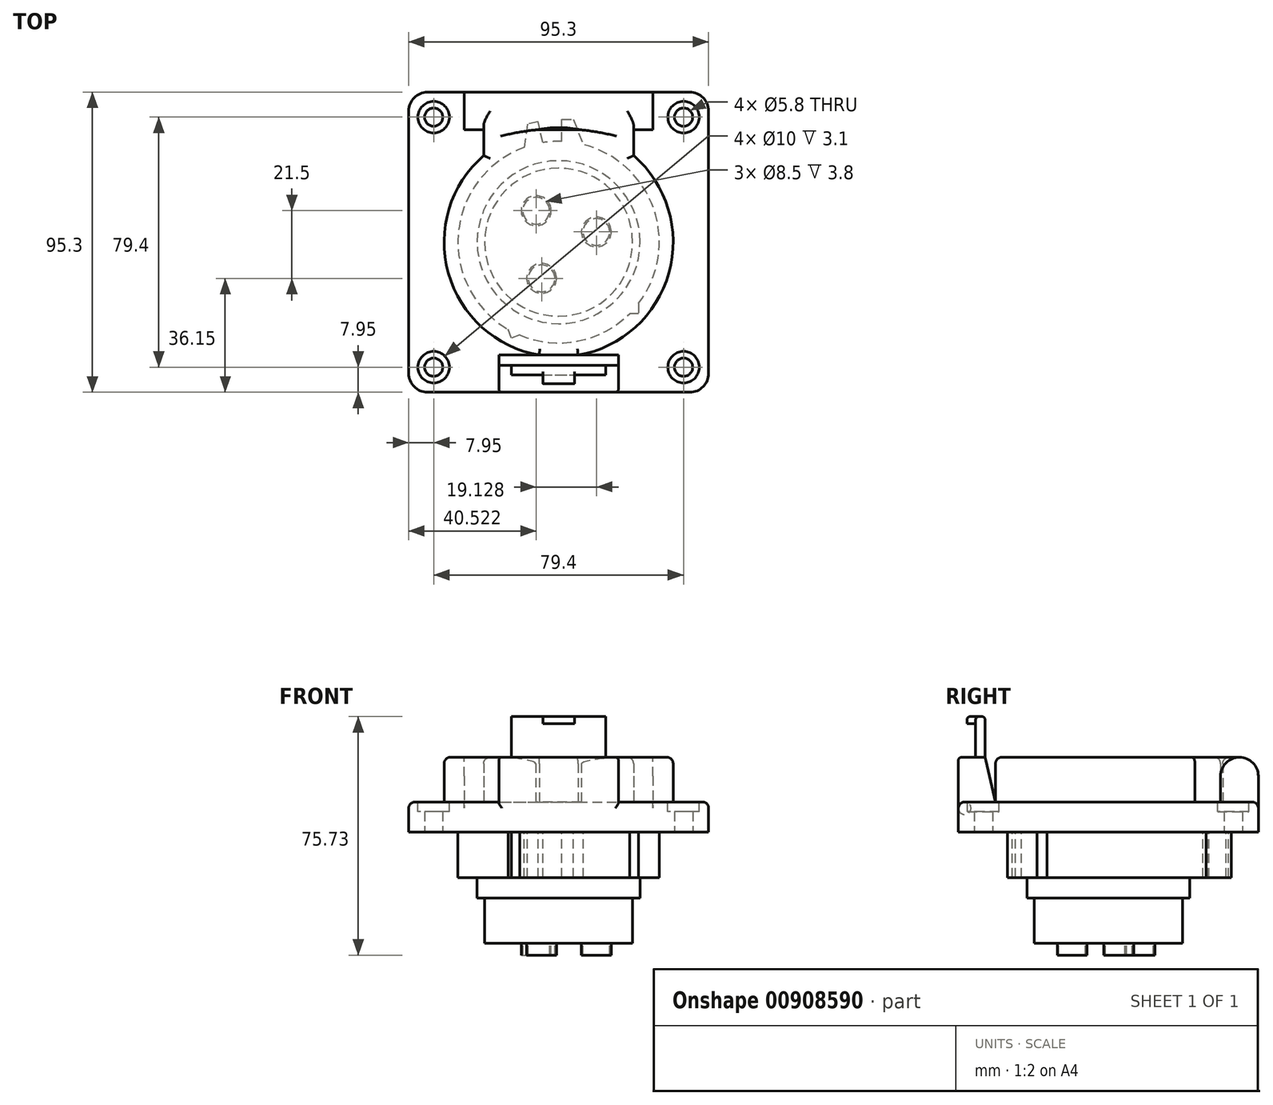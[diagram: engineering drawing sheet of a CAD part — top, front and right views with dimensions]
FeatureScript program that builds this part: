
annotation { "Feature Type Name" : "Feature", "Feature Type Description" : "" }
export const myFeature = defineFeature(function(context is Context, id is Id, definition is map)
    precondition{}
    {
        {
            var Q0;
            Q0=qCreatedBy(makeId("Top.planeOp"),FACE);
            var sketch = newSketch(context, id + "F0", { "sketchPlane" : qUnion([Q0])});
            skLineSegment(sketch, "E0.bottom", {"start": v(47.65, -47.65) * mm, "end": v(-47.65, -47.65) * mm});
            skLineSegment(sketch, "E0.top", {"start": v(47.65, 47.65) * mm, "end": v(-47.65, 47.65) * mm});
            skLineSegment(sketch, "E0.left", {"start": v(47.65, -47.65) * mm, "end": v(47.65, 47.65) * mm});
            skLineSegment(sketch, "E0.right", {"start": v(-47.65, -47.65) * mm, "end": v(-47.65, 47.65) * mm});
            skPoint(sketch, "E0.middle", {"position": v(0, 0) * mm});
            skSolve(sketch);
        }
        {
            var Q0;
            Q0=makeQuery(id+"F0.imprint","IMPRINT",FACE,{"disambiguationData":[TD([[makeQuery(id+"F0.imprint","IMPRINT",EDGE,{"derivedFrom":sQuery(id+"F0.wireOp",EDGE,"E0.bottom")}),-1.0]])]});
            extrude(context, id + "F1", {"entities" : qUnion([Q0]), "depth" : 9.5 * mm, "offsetDistance" : 25 * mm});
        }
        {
            var Q0;
            Q0=makeQuery(id+"F1.opExtrude","CAP_FACE",FACE,{"disambiguationData":[OSD([sQuery(id+"F0.wireOp",EDGE,"E0.bottom"),sQuery(id+"F0.wireOp",EDGE,"E0.top"),sQuery(id+"F0.wireOp",EDGE,"E0.left"),sQuery(id+"F0.wireOp",EDGE,"E0.right")])],"isStart":true});
            var sketch = newSketch(context, id + "F2", { "sketchPlane" : qUnion([Q0])});
            skCircle(sketch, "E1", {"center": v(0, 0) * mm, "radius": 32 * mm});
            skLineSegment(sketch, "E2", {"start": v(1.02, -31.98) * mm, "end": v(1.02, -39) * mm});
            skLineSegment(sketch, "E3", {"start": v(1.02, -39) * mm, "end": v(4.66, -39) * mm});
            skLineSegment(sketch, "E4", {"start": v(4.66, -39) * mm, "end": v(7.84, -31.02) * mm});
            skLineSegment(sketch, "E5", {"start": v(-5.04, -31.6) * mm, "end": v(-6.48, -38.2) * mm});
            skLineSegment(sketch, "E6", {"start": v(-6.48, -38.2) * mm, "end": v(-9.9, -37.45) * mm});
            skLineSegment(sketch, "E7", {"start": v(-9.9, -37.45) * mm, "end": v(-10.91, -30.08) * mm});
            skLineSegment(sketch, "E8", {"start": v(25.4, 19.47) * mm, "end": v(25.4, 22.7) * mm});
            skLineSegment(sketch, "E9", {"start": v(25.4, 22.7) * mm, "end": v(22.56, 22.7) * mm});
            skLineSegment(sketch, "E10", {"start": v(-12.39, 29.5) * mm, "end": v(-14.98, 30.5) * mm});
            skLineSegment(sketch, "E11", {"start": v(-14.98, 30.5) * mm, "end": v(-16.08, 27.67) * mm});
            skSolve(sketch);
        }
        {
            var Q0;
            {var subQ0=sQuery(id+"F2.wireOp",EDGE,"E1");var subQ5=makeQuery(id+"F2.imprint","INTERSECT",VERTEX,{"derivedFrom":[subQ0,sQuery(id+"F2.wireOp",EDGE,"E8")]});Q0=makeQuery(id+"F2.imprint","IMPRINT",FACE,{"disambiguationData":[TD([[makeQuery(id+"F2.imprint","IMPRINT",EDGE,{"disambiguationData":[TD([[subQ5,-1.0]])],"derivedFrom":subQ0}),1.0]])]});}
            var Q1;
            {var subQ0=sQuery(id+"F2.wireOp",EDGE,"E8");Q1=makeQuery(id+"F2.imprint","IMPRINT",FACE,{"disambiguationData":[TD([[makeQuery(id+"F2.imprint","IMPRINT",EDGE,{"derivedFrom":subQ0}),1.0]])]});}
            var Q2;
            {var subQ0=sQuery(id+"F2.wireOp",EDGE,"E10");Q2=makeQuery(id+"F2.imprint","IMPRINT",FACE,{"disambiguationData":[TD([[makeQuery(id+"F2.imprint","IMPRINT",EDGE,{"derivedFrom":subQ0}),1.0]])]});}
            var Q3;
            {var subQ0=sQuery(id+"F2.wireOp",EDGE,"E2");Q3=makeQuery(id+"F2.imprint","IMPRINT",FACE,{"disambiguationData":[TD([[makeQuery(id+"F2.imprint","IMPRINT",EDGE,{"derivedFrom":subQ0}),1.0]])]});}
            var Q4;
            {var subQ0=sQuery(id+"F2.wireOp",EDGE,"E5");Q4=makeQuery(id+"F2.imprint","IMPRINT",FACE,{"disambiguationData":[TD([[makeQuery(id+"F2.imprint","IMPRINT",EDGE,{"derivedFrom":subQ0}),-1.0]])]});}
            extrude(context, id + "F3", {"entities" : qUnion([Q0, Q1, Q2, Q3, Q4]), "operationType" : NewBodyOperationType.ADD, "depth" : 14.5 * mm, "offsetDistance" : 25 * mm});
        }
        {
            var Q0;
            Q0=makeQuery(id+"F3.opExtrude","CAP_FACE",FACE,{"disambiguationData":[OSD([sQuery(id+"F2.wireOp",EDGE,"E1"),sQuery(id+"F2.wireOp",EDGE,"E2"),sQuery(id+"F2.wireOp",EDGE,"E3"),sQuery(id+"F2.wireOp",EDGE,"E4"),sQuery(id+"F2.wireOp",EDGE,"E5"),sQuery(id+"F2.wireOp",EDGE,"E6"),sQuery(id+"F2.wireOp",EDGE,"E7"),sQuery(id+"F2.wireOp",EDGE,"E8"),sQuery(id+"F2.wireOp",EDGE,"E9"),sQuery(id+"F2.wireOp",EDGE,"E10"),sQuery(id+"F2.wireOp",EDGE,"E11")])],"isStart":false});
            var sketch = newSketch(context, id + "F4", { "sketchPlane" : qUnion([Q0])});
            skCircle(sketch, "E12", {"center": v(0, 0) * mm, "radius": 25.88 * mm});
            skSolve(sketch);
        }
        {
            var Q0;
            Q0 = qSketchRegion(id + "F4", true);
            extrude(context, id + "F5", {"entities" : qUnion([Q0]), "operationType" : NewBodyOperationType.ADD, "depth" : 6.5 * mm, "offsetDistance" : 25 * mm});
        }
        {
            var Q0;
            Q0=makeQuery(id+"F5.opExtrude","CAP_FACE",FACE,{"disambiguationData":[OSD([sQuery(id+"F4.wireOp",EDGE,"E12")])],"isStart":false});
            var sketch = newSketch(context, id + "F6", { "sketchPlane" : qUnion([Q0])});
            skCircle(sketch, "E13", {"center": v(0, 0) * mm, "radius": 23.5 * mm});
            skSolve(sketch);
        }
        {
            var Q0;
            Q0 = qSketchRegion(id + "F6", true);
            extrude(context, id + "F7", {"entities" : qUnion([Q0]), "operationType" : NewBodyOperationType.ADD, "depth" : 14.33 * mm, "offsetDistance" : 25 * mm});
        }
        {
            var Q0;
            Q0=makeQuery(id+"F7.opExtrude","CAP_FACE",FACE,{"disambiguationData":[OSD([sQuery(id+"F6.wireOp",EDGE,"E13")])],"isStart":false});
            var sketch = newSketch(context, id + "F8", { "sketchPlane" : qUnion([Q0])});
            skCircle(sketch, "E14", {"center": v(-7.13, -10) * mm, "radius": 4.75 * mm});
            skCircle(sketch, "E15", {"center": v(-5.4, 11.5) * mm, "radius": 4.75 * mm});
            skCircle(sketch, "E16", {"center": v(12, -3.26) * mm, "radius": 4.75 * mm});
            skCircle(sketch, "E17", {"center": v(12, -3.26) * mm, "radius": 4.25 * mm});
            skCircle(sketch, "E18", {"center": v(-7.13, -10) * mm, "radius": 4.25 * mm});
            skCircle(sketch, "E19", {"center": v(-5.4, 11.5) * mm, "radius": 4.25 * mm});
            skSolve(sketch);
        }
        {
            var Q0;
            Q0 = qSketchRegion(id + "F8", true);
            extrude(context, id + "F9", {"entities" : qUnion([Q0]), "operationType" : NewBodyOperationType.ADD, "depth" : 3.8 * mm, "offsetDistance" : 25 * mm});
        }
        {
            var Q0;
            Q0=makeQuery(id+"F1.opExtrude","CAP_FACE",FACE,{"disambiguationData":[OSD([sQuery(id+"F0.wireOp",EDGE,"E0.bottom"),sQuery(id+"F0.wireOp",EDGE,"E0.top"),sQuery(id+"F0.wireOp",EDGE,"E0.left"),sQuery(id+"F0.wireOp",EDGE,"E0.right")])],"isStart":false});
            var sketch = newSketch(context, id + "F10", { "sketchPlane" : qUnion([Q0])});
            skLineSegment(sketch, "E20.bottom", {"start": v(-30, 47.65) * mm, "end": v(30, 47.65) * mm});
            skLineSegment(sketch, "E20.top", {"start": v(-30, 35.65) * mm, "end": v(30, 35.65) * mm});
            skLineSegment(sketch, "E20.left", {"start": v(-30, 47.65) * mm, "end": v(-30, 35.65) * mm});
            skLineSegment(sketch, "E20.right", {"start": v(30, 47.65) * mm, "end": v(30, 35.65) * mm});
            skCircle(sketch, "E21", {"center": v(0, 0) * mm, "radius": 36.38 * mm});
            skLineSegment(sketch, "E22", {"start": v(-23.8, 35.65) * mm, "end": v(-23.8, 27.5) * mm});
            skLineSegment(sketch, "E23", {"start": v(23.8, 35.65) * mm, "end": v(23.8, 27.5) * mm});
            skLineSegment(sketch, "E24.bottom", {"start": v(-19, -47.65) * mm, "end": v(19, -47.65) * mm});
            skLineSegment(sketch, "E24.top", {"start": v(-19, -35.85) * mm, "end": v(19, -35.85) * mm});
            skLineSegment(sketch, "E24.left", {"start": v(-19, -47.65) * mm, "end": v(-19, -35.85) * mm});
            skLineSegment(sketch, "E24.right", {"start": v(19, -47.65) * mm, "end": v(19, -35.85) * mm});
            skSolve(sketch);
        }
        {
            var Q0;
            Q0 = qSketchRegion(id + "F10", true);
            var Q1;
            {var subQ0=sQuery(id+"F10.wireOp",EDGE,"E21");var subQ1=sQuery(id+"F10.wireOp",EDGE,"E20.top");var subQ2=makeQuery(id+"F10.imprint","INTERSECT",VERTEX,{"disambiguationData":[OD(0.0)],"derivedFrom":[subQ1,subQ0]});Q1=makeQuery(id+"F10.imprint","IMPRINT",FACE,{"disambiguationData":[TD([[makeQuery(id+"F10.imprint","IMPRINT",EDGE,{"disambiguationData":[TD([[subQ2,-1.0]])],"derivedFrom":subQ1}),1.0]])]});}
            extrude(context, id + "F11", {"entities" : qUnion([Q0, Q1]), "operationType" : NewBodyOperationType.ADD, "depth" : 14.2 * mm, "offsetDistance" : 25 * mm});
        }
        {
            var Q0;
            Q0=makeQuery(id+"F11.opExtrude","SWEPT_FACE",FACE,{"disambiguationData":[OSD([sQuery(id+"F10.wireOp",EDGE,"E24.right")])]});
            var sketch = newSketch(context, id + "F12", { "sketchPlane" : qUnion([Q0])});
            skLineSegment(sketch, "E25", {"start": v(-35.85, 9.5) * mm, "end": v(-39.17, 23.7) * mm});
            skSolve(sketch);
        }
        {
            var Q0;
            {var subQ0=sQuery(id+"F12.wireOp",EDGE,"E25");Q0=makeQuery(id+"F12.imprint","IMPRINT",FACE,{"disambiguationData":[TD([[makeQuery(id+"F12.imprint","IMPRINT",EDGE,{"derivedFrom":subQ0}),-1.0]])]});}
            extrude(context, id + "F13", {"entities" : qUnion([Q0]), "operationType" : NewBodyOperationType.REMOVE, "endBound" : BoundingType.THROUGH_ALL, "oppositeDirection" : true, "depth" : 25 * mm, "offsetDistance" : 25 * mm});
        }
        {
            var Q0;
            {var subQ0=sQuery(id+"F10.wireOp",EDGE,"E24.right");var subQ1=sQuery(id+"F10.wireOp",EDGE,"E24.left");var subQ2=sQuery(id+"F10.wireOp",EDGE,"E24.bottom");Q0=makeQuery(id+"F13.boolean.opBoolean","SPLIT",FACE,{"disambiguationData":[TD([makeQuery(id+"F1.opExtrude","SWEPT_FACE",FACE,{"disambiguationData":[OSD([sQuery(id+"F0.wireOp",EDGE,"E0.bottom")])]})])],"derivedFrom":makeQuery(id+"F11.opExtrude","CAP_FACE",FACE,{"disambiguationData":[OSD([sQuery(id+"F10.wireOp",EDGE,"E20.bottom"),sQuery(id+"F10.wireOp",EDGE,"E20.top"),sQuery(id+"F10.wireOp",EDGE,"E20.left"),sQuery(id+"F10.wireOp",EDGE,"E20.right"),sQuery(id+"F10.wireOp",EDGE,"E21"),sQuery(id+"F10.wireOp",EDGE,"E22"),sQuery(id+"F10.wireOp",EDGE,"E23"),subQ2,sQuery(id+"F10.wireOp",EDGE,"E24.top"),subQ1,subQ0])],"isStart":false})});}
            var sketch = newSketch(context, id + "F14", { "sketchPlane" : qUnion([Q0])});
            skLineSegment(sketch, "E26.bottom", {"start": v(-15, -39.17) * mm, "end": v(15, -39.17) * mm});
            skLineSegment(sketch, "E26.top", {"start": v(-15, -42.17) * mm, "end": v(15, -42.17) * mm});
            skLineSegment(sketch, "E26.left", {"start": v(-15, -39.17) * mm, "end": v(-15, -42.17) * mm});
            skLineSegment(sketch, "E26.right", {"start": v(15, -39.17) * mm, "end": v(15, -42.17) * mm});
            skLineSegment(sketch, "E27.bottom", {"start": v(-5, -42.17) * mm, "end": v(5, -42.17) * mm});
            skLineSegment(sketch, "E27.top", {"start": v(-5, -44.92) * mm, "end": v(5, -44.92) * mm});
            skLineSegment(sketch, "E27.left", {"start": v(-5, -42.17) * mm, "end": v(-5, -44.92) * mm});
            skLineSegment(sketch, "E27.right", {"start": v(5, -42.17) * mm, "end": v(5, -44.92) * mm});
            skSolve(sketch);
        }
        {
            var Q0;
            Q0 = qSketchRegion(id + "F14", true);
            extrude(context, id + "F15", {"entities" : qUnion([Q0]), "operationType" : NewBodyOperationType.ADD, "depth" : 12.9 * mm, "offsetDistance" : 25 * mm});
        }
        {
            var Q0;
            Q0=makeQuery(id+"F15.opExtrude","SWEPT_FACE",FACE,{"disambiguationData":[OSD([sQuery(id+"F14.wireOp",EDGE,"E27.top")])]});
            var sketch = newSketch(context, id + "F16", { "sketchPlane" : qUnion([Q0])});
            skLineSegment(sketch, "E28.bottom", {"start": v(-5, 23.7) * mm, "end": v(5, 23.7) * mm});
            skLineSegment(sketch, "E28.top", {"start": v(-5, 34.34) * mm, "end": v(5, 34.34) * mm});
            skLineSegment(sketch, "E28.left", {"start": v(-5, 23.7) * mm, "end": v(-5, 34.34) * mm});
            skLineSegment(sketch, "E28.right", {"start": v(5, 23.7) * mm, "end": v(5, 34.34) * mm});
            skSolve(sketch);
        }
        {
            var Q0;
            Q0 = qSketchRegion(id + "F16", true);
            extrude(context, id + "F17", {"entities" : qUnion([Q0]), "operationType" : NewBodyOperationType.REMOVE, "oppositeDirection" : true, "depth" : 2.75 * mm, "offsetDistance" : 25 * mm});
        }
        {
            var Q0;
            {var subQ0=sQuery(id+"F10.wireOp",EDGE,"E20.top");Q0=makeQuery(id+"F11.opExtrude","CAP_EDGE",EDGE,{"disambiguationData":[OSD([subQ0]),TDD([makeQuery(id+"F10.imprint","IMPRINT",EDGE,{"disambiguationData":[TD([[makeQuery(id+"F10.imprint","INTERSECT",VERTEX,{"derivedFrom":[subQ0,sQuery(id+"F10.wireOp",EDGE,"E20.left")]}),-1.0]])],"derivedFrom":subQ0})])],"isStart":false});}
            var Q1;
            Q1=makeQuery(id+"F11.opExtrude","CAP_EDGE",EDGE,{"disambiguationData":[OSD([sQuery(id+"F10.wireOp",EDGE,"E20.bottom")])],"isStart":false});
            var Q2;
            {var subQ0=sQuery(id+"F10.wireOp",EDGE,"E20.top");Q2=makeQuery(id+"F11.opExtrude","CAP_EDGE",EDGE,{"disambiguationData":[OSD([subQ0]),TDD([makeQuery(id+"F10.imprint","IMPRINT",EDGE,{"disambiguationData":[TD([[makeQuery(id+"F10.imprint","INTERSECT",VERTEX,{"derivedFrom":[subQ0,sQuery(id+"F10.wireOp",EDGE,"E20.right")]}),1.0]])],"derivedFrom":subQ0})])],"isStart":false});}
            var Q3;
            Q3=makeQuery(id+"F1.opExtrude","SWEPT_EDGE",EDGE,{"disambiguationData":[OSD([sQuery(id+"F0.wireOp",EDGE,"E0.top"),sQuery(id+"F0.wireOp",EDGE,"E0.right")])]});
            var Q4;
            Q4=makeQuery(id+"F1.opExtrude","SWEPT_EDGE",EDGE,{"disambiguationData":[OSD([sQuery(id+"F0.wireOp",EDGE,"E0.bottom"),sQuery(id+"F0.wireOp",EDGE,"E0.right")])]});
            var Q5;
            Q5=makeQuery(id+"F1.opExtrude","SWEPT_EDGE",EDGE,{"disambiguationData":[OSD([sQuery(id+"F0.wireOp",EDGE,"E0.bottom"),sQuery(id+"F0.wireOp",EDGE,"E0.left")])]});
            var Q6;
            Q6=makeQuery(id+"F1.opExtrude","SWEPT_EDGE",EDGE,{"disambiguationData":[OSD([sQuery(id+"F0.wireOp",EDGE,"E0.top"),sQuery(id+"F0.wireOp",EDGE,"E0.left")])]});
            fillet(context, id + "F18", {"entities" : qUnion([Q0, Q1, Q2, Q3, Q4, Q5, Q6]), "radius" : 6 * mm, "tangentPropagation" : true, "allowEdgeOverflow" : false});
        }
        {
            var Q0;
            {var subQ0=sQuery(id+"F0.wireOp",EDGE,"E0.right");var subQ1=sQuery(id+"F0.wireOp",EDGE,"E0.bottom");Q0=makeQuery(id+"F11.boolean.opBoolean","SPLIT",EDGE,{"disambiguationData":[TD([makeQuery(id+"F1.opExtrude","SWEPT_FACE",FACE,{"disambiguationData":[OSD([subQ0])]})])],"derivedFrom":makeQuery(id+"F1.opExtrude","CAP_EDGE",EDGE,{"disambiguationData":[OSD([subQ1])],"isStart":false})});}
            var Q1;
            {var subQ0=sQuery(id+"F0.wireOp",EDGE,"E0.left");var subQ1=sQuery(id+"F0.wireOp",EDGE,"E0.bottom");Q1=makeQuery(id+"F11.boolean.opBoolean","SPLIT",EDGE,{"disambiguationData":[TD([makeQuery(id+"F1.opExtrude","SWEPT_FACE",FACE,{"disambiguationData":[OSD([subQ0])]})])],"derivedFrom":makeQuery(id+"F1.opExtrude","CAP_EDGE",EDGE,{"disambiguationData":[OSD([subQ1])],"isStart":false})});}
            var Q2;
            {var subQ0=sQuery(id+"F12.wireOp",EDGE,"E25");var subQ1=sQuery(id+"F10.wireOp",EDGE,"E24.right");Q2=makeQuery(id+"F15.boolean.opBoolean","SPLIT",EDGE,{"disambiguationData":[TD([makeQuery(id+"F11.opExtrude","SWEPT_FACE",FACE,{"disambiguationData":[OSD([subQ1])]})])],"derivedFrom":makeQuery(id+"F13.boolean.opBoolean","COPY",EDGE,{"derivedFrom":makeQuery(id+"F13.opExtrude","SWEPT_EDGE",EDGE,{"disambiguationData":[OSD([subQ1,subQ0])]})})});}
            var Q3;
            {var subQ0=sQuery(id+"F12.wireOp",EDGE,"E25");var subQ1=sQuery(id+"F10.wireOp",EDGE,"E24.left");var subQ2=sQuery(id+"F10.wireOp",EDGE,"E24.right");Q3=makeQuery(id+"F15.boolean.opBoolean","SPLIT",EDGE,{"disambiguationData":[TD([makeQuery(id+"F11.opExtrude","SWEPT_FACE",FACE,{"disambiguationData":[OSD([subQ1])]})])],"derivedFrom":makeQuery(id+"F13.boolean.opBoolean","COPY",EDGE,{"derivedFrom":makeQuery(id+"F13.opExtrude","SWEPT_EDGE",EDGE,{"disambiguationData":[OSD([subQ2,subQ0])]})})});}
            var Q4;
            {var subQ0=sQuery(id+"F10.wireOp",EDGE,"E23");var subQ1=sQuery(id+"F10.wireOp",EDGE,"E22");var subQ2=sQuery(id+"F10.wireOp",EDGE,"E21");var subQ3=sQuery(id+"F10.wireOp",EDGE,"E24.top");var subQ4=sQuery(id+"F10.wireOp",EDGE,"E20.right");var subQ5=sQuery(id+"F10.wireOp",EDGE,"E20.left");var subQ6=sQuery(id+"F10.wireOp",EDGE,"E24.right");var subQ7=sQuery(id+"F10.wireOp",EDGE,"E20.top");var subQ8=sQuery(id+"F10.wireOp",EDGE,"E20.bottom");Q4=makeQuery(id+"F13.boolean.opBoolean","SPLIT",FACE,{"disambiguationData":[TD([makeQuery(id+"F1.opExtrude","SWEPT_FACE",FACE,{"disambiguationData":[OSD([sQuery(id+"F0.wireOp",EDGE,"E0.top")])]})])],"derivedFrom":makeQuery(id+"F11.opExtrude","CAP_FACE",FACE,{"disambiguationData":[OSD([subQ8,subQ7,subQ5,subQ4,subQ2,subQ1,subQ0,sQuery(id+"F10.wireOp",EDGE,"E24.bottom"),subQ3,sQuery(id+"F10.wireOp",EDGE,"E24.left"),subQ6])],"isStart":false})});}
            fillet(context, id + "F19", {"entities" : qUnion([Q0, Q1, Q2, Q3, Q4]), "radius" : 2 * mm, "tangentPropagation" : true, "allowEdgeOverflow" : false});
        }
        {
            var Q0;
            Q0=makeQuery(id+"F11.opExtrude","SWEPT_EDGE",EDGE,{"disambiguationData":[OSD([sQuery(id+"F0.wireOp",EDGE,"E0.bottom"),sQuery(id+"F10.wireOp",EDGE,"E24.bottom"),sQuery(id+"F10.wireOp",EDGE,"E24.left")])]});
            var Q1;
            Q1=makeQuery(id+"F11.opExtrude","CAP_EDGE",EDGE,{"disambiguationData":[OSD([sQuery(id+"F10.wireOp",EDGE,"E24.bottom")])],"isStart":false});
            var Q2;
            Q2=makeQuery(id+"F11.opExtrude","CAP_EDGE",EDGE,{"disambiguationData":[OSD([sQuery(id+"F10.wireOp",EDGE,"E24.left")])],"isStart":false});
            var Q3;
            Q3=makeQuery(id+"F11.opExtrude","CAP_EDGE",EDGE,{"disambiguationData":[OSD([sQuery(id+"F10.wireOp",EDGE,"E24.right")])],"isStart":false});
            var Q4;
            Q4=makeQuery(id+"F11.opExtrude","SWEPT_EDGE",EDGE,{"disambiguationData":[OSD([sQuery(id+"F0.wireOp",EDGE,"E0.bottom"),sQuery(id+"F10.wireOp",EDGE,"E24.bottom"),sQuery(id+"F10.wireOp",EDGE,"E24.right")])]});
            var Q5;
            {var subQ0=sQuery(id+"F14.wireOp",EDGE,"E26.top");Q5=makeQuery(id+"F15.opExtrude","CAP_EDGE",EDGE,{"disambiguationData":[OSD([subQ0]),TDD([makeQuery(id+"F14.imprint","IMPRINT",EDGE,{"disambiguationData":[TD([[makeQuery(id+"F14.imprint","INTERSECT",VERTEX,{"derivedFrom":[subQ0,sQuery(id+"F14.wireOp",EDGE,"E26.left")]}),-1.0]])],"derivedFrom":subQ0})])],"isStart":false});}
            var Q6;
            {var subQ0=sQuery(id+"F14.wireOp",EDGE,"E26.top");Q6=makeQuery(id+"F15.opExtrude","CAP_EDGE",EDGE,{"disambiguationData":[OSD([subQ0]),TDD([makeQuery(id+"F14.imprint","IMPRINT",EDGE,{"disambiguationData":[TD([[makeQuery(id+"F14.imprint","INTERSECT",VERTEX,{"derivedFrom":[subQ0,sQuery(id+"F14.wireOp",EDGE,"E26.right")]}),1.0]])],"derivedFrom":subQ0})])],"isStart":false});}
            var Q7;
            Q7=makeQuery(id+"F15.opExtrude","CAP_EDGE",EDGE,{"disambiguationData":[OSD([sQuery(id+"F14.wireOp",EDGE,"E26.bottom")])],"isStart":false});
            var Q8;
            Q8=makeQuery(id+"F17.boolean.opBoolean","COPY",EDGE,{"derivedFrom":makeQuery(id+"F17.opExtrude","CAP_EDGE",EDGE,{"disambiguationData":[OSD([sQuery(id+"F16.wireOp",EDGE,"E28.top")])],"isStart":true})});
            var Q9;
            Q9=makeQuery(id+"F15.opExtrude","CAP_EDGE",EDGE,{"disambiguationData":[OSD([sQuery(id+"F14.wireOp",EDGE,"E27.top")])],"isStart":false});
            fillet(context, id + "F20", {"entities" : qUnion([Q0, Q1, Q2, Q3, Q4, Q5, Q6, Q7, Q8, Q9]), "radius" : 1 * mm, "tangentPropagation" : true, "allowEdgeOverflow" : false});
        }
        {
            var Q0;
            Q0=makeQuery(id+"F1.opExtrude","CAP_FACE",FACE,{"disambiguationData":[OSD([sQuery(id+"F0.wireOp",EDGE,"E0.bottom"),sQuery(id+"F0.wireOp",EDGE,"E0.top"),sQuery(id+"F0.wireOp",EDGE,"E0.left"),sQuery(id+"F0.wireOp",EDGE,"E0.right")])],"isStart":true});
            var sketch = newSketch(context, id + "F21", { "sketchPlane" : qUnion([Q0])});
            skCircle(sketch, "E29", {"center": v(39.7, 39.7) * mm, "radius": 2.9 * mm});
            skCircle(sketch, "E30.MirrorC", {"center": v(-39.7, 39.7) * mm, "radius": 2.9 * mm});
            skCircle(sketch, "E31.MirrorC", {"center": v(39.7, -39.7) * mm, "radius": 2.9 * mm});
            skCircle(sketch, "E32.MirrorC", {"center": v(-39.7, -39.7) * mm, "radius": 2.9 * mm});
            skSolve(sketch);
        }
        {
            var Q0;
            Q0 = qSketchRegion(id + "F21", true);
            extrude(context, id + "F22", {"entities" : qUnion([Q0]), "operationType" : NewBodyOperationType.REMOVE, "endBound" : BoundingType.THROUGH_ALL, "oppositeDirection" : true, "depth" : 25 * mm, "offsetDistance" : 25 * mm});
        }
        {
            var Q0;
            {var subQ7=sQuery(id+"F0.wireOp",EDGE,"E0.bottom");var subQ8=sQuery(id+"F0.wireOp",EDGE,"E0.right");var subQ9=sQuery(id+"F0.wireOp",EDGE,"E0.top");Q0=makeQuery(id+"F11.boolean.opBoolean","SPLIT",FACE,{"disambiguationData":[TD([makeQuery(id+"F1.opExtrude","SWEPT_FACE",FACE,{"disambiguationData":[OSD([subQ8])]})])],"derivedFrom":makeQuery(id+"F1.opExtrude","CAP_FACE",FACE,{"disambiguationData":[OSD([subQ7,subQ9,sQuery(id+"F0.wireOp",EDGE,"E0.left"),subQ8])],"isStart":false})});}
            var sketch = newSketch(context, id + "F23", { "sketchPlane" : qUnion([Q0])});
            skCircle(sketch, "E33", {"center": v(-39.7, 39.7) * mm, "radius": 5 * mm});
            skCircle(sketch, "E34", {"center": v(-39.7, -39.7) * mm, "radius": 5 * mm});
            skCircle(sketch, "E35.MirrorC", {"center": v(39.7, 39.7) * mm, "radius": 5 * mm});
            skCircle(sketch, "E36.MirrorC", {"center": v(39.7, -39.7) * mm, "radius": 5 * mm});
            skSolve(sketch);
        }
        {
            var Q0;
            Q0 = qSketchRegion(id + "F23", true);
            extrude(context, id + "F24", {"entities" : qUnion([Q0]), "operationType" : NewBodyOperationType.REMOVE, "oppositeDirection" : true, "depth" : 3.1 * mm, "offsetDistance" : 25 * mm});
        }
    });
